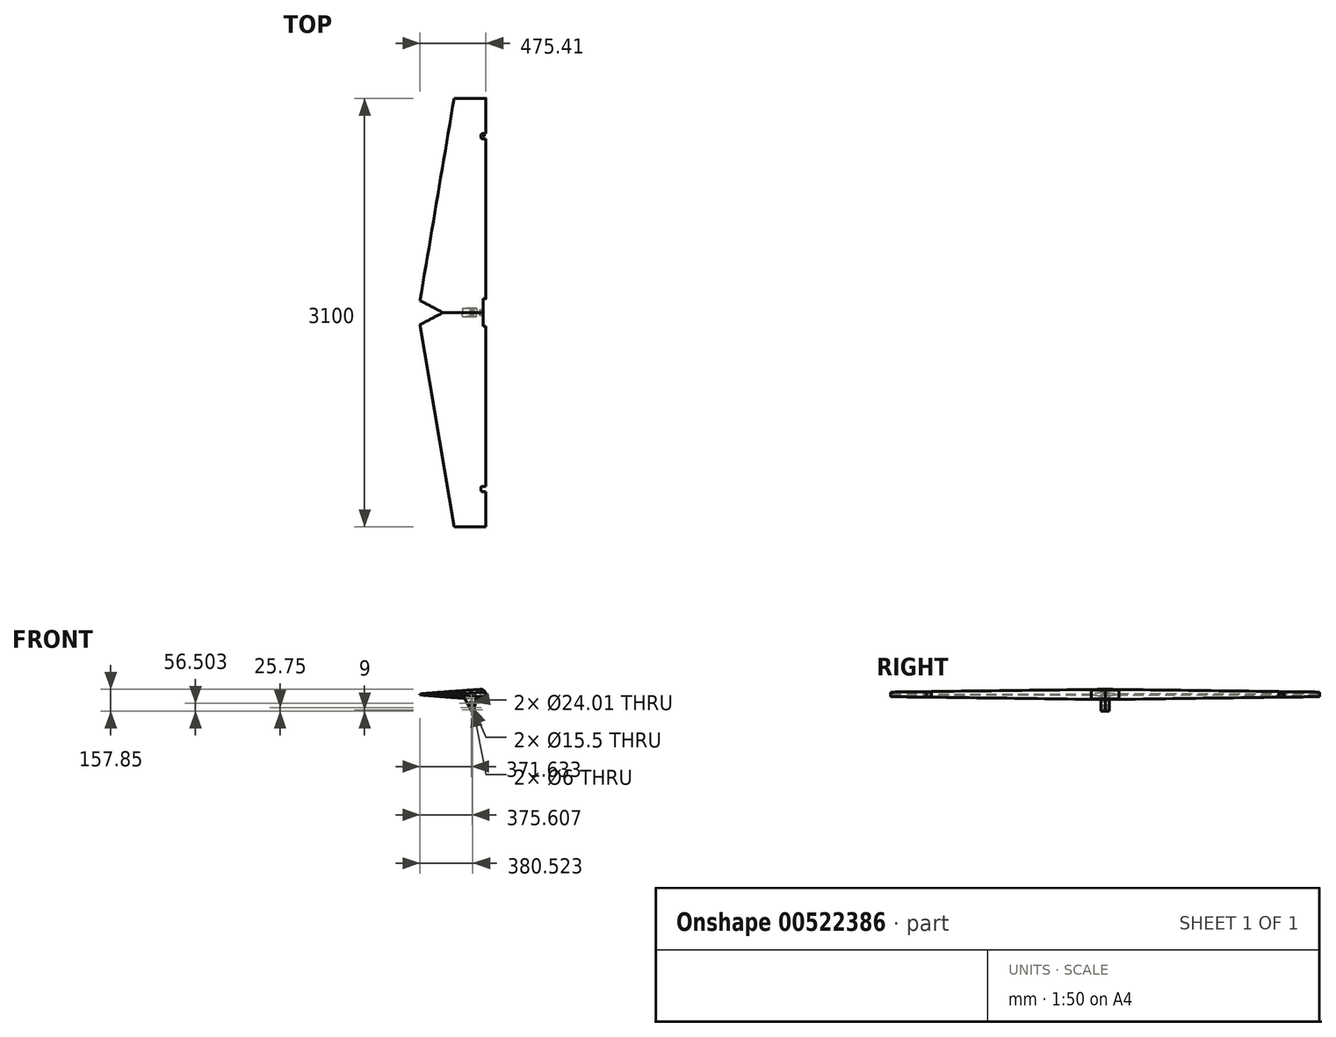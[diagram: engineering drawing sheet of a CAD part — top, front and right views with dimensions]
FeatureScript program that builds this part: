
annotation { "Feature Type Name" : "Feature", "Feature Type Description" : "" }
export const myFeature = defineFeature(function(context is Context, id is Id, definition is map)
    precondition{}
    {
        {
            var Q0;
            Q0=qCreatedBy(makeId("Top.planeOp"),FACE);
            var sketch = newSketch(context, id + "F0", { "sketchPlane" : qUnion([Q0])});
            skLineSegment(sketch, "E0.bottom", {"start": v(0, 0) * mm, "end": v(-490, 0) * mm});
            skLineSegment(sketch, "E0.top", {"start": v(0, -1550) * mm, "end": v(-230, -1550) * mm});
            skLineSegment(sketch, "E0.left", {"start": v(0, 0) * mm, "end": v(0, -1550) * mm});
            skLineSegment(sketch, "E0.right", {"start": v(-490, 0) * mm, "end": v(-230, -1550) * mm});
            skLineSegment(sketch, "E1", {"start": v(0, -100) * mm, "end": v(-20, -100) * mm});
            skLineSegment(sketch, "E2", {"start": v(-20, -100) * mm, "end": v(-20, 0) * mm});
            skLineSegment(sketch, "E3", {"start": v(-310, 0) * mm, "end": v(-475.4, -87) * mm});
            skLineSegment(sketch, "E4.bottom", {"start": v(0, -1295) * mm, "end": v(-36, -1295) * mm});
            skLineSegment(sketch, "E4.top", {"start": v(0, -1257) * mm, "end": v(-36, -1257) * mm});
            skLineSegment(sketch, "E4.left", {"start": v(0, -1295) * mm, "end": v(0, -1257) * mm});
            skLineSegment(sketch, "E4.right", {"start": v(-36, -1295) * mm, "end": v(-36, -1257) * mm});
            skSolve(sketch);
        }
        {
            var Q0;
            Q0=qCreatedBy(makeId("Front.planeOp"),FACE);
            var sketch = newSketch(context, id + "F1", { "sketchPlane" : qUnion([Q0])});
            skLineSegment(sketch, "E5", {"start": v(-39.56, 36.75) * mm, "end": v(-490, 3.5) * mm});
            skLineSegment(sketch, "E6", {"start": v(-490, 3.5) * mm, "end": v(-490, -3.5) * mm});
            skLineSegment(sketch, "E7", {"start": v(-490, -3.5) * mm, "end": v(-39.56, -36.75) * mm});
            skArc(sketch, "E8", {"start": v(-39.56, -36.75) * mm, "mid": v(0, 0) * mm, "end": v(-39.56, 36.75) * mm});
            skCircle(sketch, "E9", {"center": v(-36.85, 0) * mm, "radius": 5 * mm, "construction": true});
            skSolve(sketch);
        }
        {
            var Q0;
            Q0=sQuery(id+"F0.wireOp",VERTEX,"E0.left.end");
            var Q1;
            Q1=sQuery(id+"F0.wireOp",EDGE,"E0.left");
            cPlane(context, id + "F2", {"entities" : qUnion([Q0, Q1]), "cplaneType" : CPlaneType.LINE_POINT, "offset" : 25 * mm, "width" : 150 * mm, "height" : 150 * mm});
        }
        {
            var Q0;
            Q0=qCreatedBy(id+"F2.planeOp",FACE);
            var sketch = newSketch(context, id + "F3", { "sketchPlane" : qUnion([Q0])});
            skLineSegment(sketch, "E10", {"start": v(-17.62, 16.5) * mm, "end": v(-230, 2.5) * mm});
            skLineSegment(sketch, "E11", {"start": v(-230, 2.5) * mm, "end": v(-230, -2.5) * mm});
            skLineSegment(sketch, "E12", {"start": v(-230, -2.5) * mm, "end": v(-17.62, -16.5) * mm});
            skArc(sketch, "E13", {"start": v(-17.62, -16.5) * mm, "mid": v(0, 0) * mm, "end": v(-17.62, 16.5) * mm});
            skSolve(sketch);
        }
        {
            var Q0;
            Q0=makeQuery(id+"F3.imprint","IMPRINT",FACE,{"disambiguationData":[TD([[makeQuery(id+"F3.imprint","IMPRINT",EDGE,{"derivedFrom":sQuery(id+"F3.wireOp",EDGE,"E10")}),1.0]])]});
            var Q1;
            Q1=makeQuery(id+"F1.imprint","IMPRINT",FACE,{"disambiguationData":[TD([[makeQuery(id+"F1.imprint","IMPRINT",EDGE,{"derivedFrom":sQuery(id+"F1.wireOp",EDGE,"E5")}),1.0]])]});
            loft(context, id + "F4", {"sheetProfilesArray" : [{ "sheetProfileEntities" : qUnion([Q0]) }, { "sheetProfileEntities" : qUnion([Q1]) }]});
        }
        {
            var Q0;
            {var subQ4=sQuery(id+"F0.wireOp",EDGE,"E1");Q0=makeQuery(id+"F0.imprint","IMPRINT",FACE,{"disambiguationData":[TD([[makeQuery(id+"F0.imprint","IMPRINT",EDGE,{"derivedFrom":subQ4}),-1.0]])]});}
            extrude(context, id + "F5", {"entities" : qUnion([Q0]), "operationType" : NewBodyOperationType.REMOVE, "endBound" : BoundingType.SYMMETRIC, "depth" : 100 * mm, "offsetDistance" : 25 * mm});
        }
        {
            var Q0;
            {var subQ3=sQuery(id+"F0.wireOp",EDGE,"E3");Q0=makeQuery(id+"F0.imprint","IMPRINT",FACE,{"disambiguationData":[TD([[makeQuery(id+"F0.imprint","IMPRINT",EDGE,{"derivedFrom":subQ3}),-1.0]])]});}
            var Q1;
            Q1=sQuery(id+"F0.wireOp",EDGE,"E3");
            var Q2;
            Q2=sQuery(id+"F0.wireOp",EDGE,"E0.bottom");
            var Q3;
            Q3=sQuery(id+"F0.wireOp",EDGE,"E0.right");
            extrude(context, id + "F6", {"entities" : qUnion([Q0]), "operationType" : NewBodyOperationType.REMOVE, "surfaceEntities" : qUnion([Q1, Q2, Q3]), "endBound" : BoundingType.SYMMETRIC, "oppositeDirection" : true, "depth" : 60 * mm, "offsetDistance" : 25 * mm});
        }
        {
            var Q0;
            Q0=qCreatedBy(makeId("Front.planeOp"),FACE);
            var sketch = newSketch(context, id + "F7", { "sketchPlane" : qUnion([Q0])});
            skLineSegment(sketch, "E14", {"start": v(-66, 0) * mm, "end": v(-169, 0) * mm});
            skLineSegment(sketch, "E15", {"start": v(-169, 0) * mm, "end": v(-102.34, -121) * mm});
            skLineSegment(sketch, "E16", {"start": v(-102.34, -121) * mm, "end": v(-87.34, -121) * mm});
            skLineSegment(sketch, "E17", {"start": v(-87.34, -121) * mm, "end": v(-66, 0) * mm});
            skCircle(sketch, "E18", {"center": v(-38.5, 0) * mm, "radius": 5 * mm});
            skCircle(sketch, "E19", {"center": v(-103.78, -64.5) * mm, "radius": 12 * mm});
            skCircle(sketch, "E20", {"center": v(-99.8, -95.25) * mm, "radius": 7.75 * mm});
            skCircle(sketch, "E21", {"center": v(-94.89, -112) * mm, "radius": 3 * mm});
            skSolve(sketch);
        }
        {
            var Q0;
            Q0=makeQuery(id+"F7.imprint","IMPRINT",FACE,{"disambiguationData":[TD([[makeQuery(id+"F7.imprint","IMPRINT",EDGE,{"derivedFrom":sQuery(id+"F7.wireOp",EDGE,"E18")}),1.0]])]});
            extrude(context, id + "F8", {"entities" : qUnion([Q0]), "operationType" : NewBodyOperationType.ADD, "oppositeDirection" : true, "depth" : 19 * mm, "offsetDistance" : 25 * mm});
        }
        {
            var Q0;
            Q0=makeQuery(id+"F7.imprint","IMPRINT",FACE,{"disambiguationData":[TD([[makeQuery(id+"F7.imprint","IMPRINT",EDGE,{"derivedFrom":sQuery(id+"F7.wireOp",EDGE,"E14")}),1.0]])]});
            extrude(context, id + "F9", {"entities" : qUnion([Q0]), "operationType" : NewBodyOperationType.ADD, "oppositeDirection" : true, "depth" : 30 * mm, "offsetDistance" : 25 * mm});
        }
        {
            var Q0;
            Q0=qCreatedBy(id+"F2.planeOp",FACE);
            cPlane(context, id + "F10", {"entities" : qUnion([Q0]), "cplaneType" : CPlaneType.OFFSET, "offset" : 520 * mm, "oppositeDirection" : true, "width" : 150 * mm, "height" : 150 * mm});
        }
        {
            var Q0;
            Q0=makeQuery(id+"F0.imprint","IMPRINT",FACE,{"disambiguationData":[TD([[makeQuery(id+"F0.imprint","IMPRINT",EDGE,{"derivedFrom":sQuery(id+"F0.wireOp",EDGE,"E4.bottom")}),-1.0]])]});
            extrude(context, id + "F11", {"entities" : qUnion([Q0]), "operationType" : NewBodyOperationType.REMOVE, "endBound" : BoundingType.SYMMETRIC, "depth" : 100 * mm, "offsetDistance" : 25 * mm});
        }
        {
            var Q0;
            Q0=makeQuery(id+"F11.boolean.opBoolean","COPY",EDGE,{"derivedFrom":makeQuery(id+"F11.opExtrude","SWEPT_EDGE",EDGE,{"disambiguationData":[OSD([sQuery(id+"F0.wireOp",EDGE,"E4.bottom"),sQuery(id+"F0.wireOp",EDGE,"E4.right")])]})});
            var Q1;
            Q1=makeQuery(id+"F11.boolean.opBoolean","COPY",EDGE,{"derivedFrom":makeQuery(id+"F11.opExtrude","SWEPT_EDGE",EDGE,{"disambiguationData":[OSD([sQuery(id+"F0.wireOp",EDGE,"E4.top"),sQuery(id+"F0.wireOp",EDGE,"E4.right")])]})});
            fillet(context, id + "F12", {"entities" : qUnion([Q0, Q1]), "radius" : 12 * mm, "tangentPropagation" : true, "allowEdgeOverflow" : false});
        }
        {
            var Q0;
            Q0=makeQuery(id+"F4.opLoft","SWEPT_BODY",BODY,{"disambiguationData":[OSD([makeQuery(id+"F1.imprint","IMPRINT",FACE,{"disambiguationData":[TD([[makeQuery(id+"F1.imprint","IMPRINT",EDGE,{"derivedFrom":sQuery(id+"F1.wireOp",EDGE,"E5")}),1.0]])]}),makeQuery(id+"F3.imprint","IMPRINT",FACE,{"disambiguationData":[TD([[makeQuery(id+"F3.imprint","IMPRINT",EDGE,{"derivedFrom":sQuery(id+"F3.wireOp",EDGE,"E10")}),1.0]])]})])]});
            var Q1;
            Q1=qCreatedBy(makeId("Front.planeOp"),FACE);
            mirror(context, id + "F13", {"entities" : qUnion([Q0]), "mirrorPlane" : qUnion([Q1])});
        }
        {
            var Q0;
            Q0=makeQuery(id+"F13.opPattern","COPY",FACE,{"derivedFrom":makeQuery(id+"F11.boolean.opBoolean","COPY",FACE,{"derivedFrom":makeQuery(id+"F11.opExtrude","SWEPT_FACE",FACE,{"disambiguationData":[OSD([sQuery(id+"F0.wireOp",EDGE,"E4.bottom")])]})}),"instanceName":"1"});
            var sketch = newSketch(context, id + "F14", { "sketchPlane" : qUnion([Q0])});
            skCircle(sketch, "E22", {"center": v(-14, 0) * mm, "radius": 5 * mm});
            skFitSpline(sketch, "E23.0", {"points": [v(-36, 18.82) * mm, v(-31.07, 19.16) * mm, v(-26.15, 19.5) * mm, v(-19.87, 19.92) * mm, v(-18.5, 19.88) * mm, v(-15.8, 19.5) * mm, v(-14.47, 19.18) * mm, v(-11.91, 18.26) * mm, v(-10.68, 17.67) * mm, v(-8.36, 16.26) * mm, v(-7.28, 15.43) * mm, v(-5.3, 13.58) * mm, v(-4.4, 12.55) * mm, v(-2.84, 10.33) * mm, v(-2.18, 9.14) * mm, v(-1.1, 6.66) * mm, v(-0.69, 5.36) * mm, v(-0.14, 2.7) * mm, v(0, 1.35) * mm, v(0, -1.35) * mm, v(-0.14, -2.7) * mm, v(-0.69, -5.36) * mm, v(-1.1, -6.66) * mm, v(-2.18, -9.14) * mm, v(-2.84, -10.33) * mm, v(-4.4, -12.55) * mm, v(-5.3, -13.58) * mm, v(-7.28, -15.43) * mm, v(-8.36, -16.26) * mm, v(-10.68, -17.67) * mm, v(-11.91, -18.26) * mm, v(-14.47, -19.18) * mm, v(-15.8, -19.5) * mm, v(-18.5, -19.88) * mm, v(-19.87, -19.92) * mm, v(-26.15, -19.5) * mm, v(-31.07, -19.16) * mm, v(-36, -18.82) * mm]});
            skFitSpline(sketch, "E24", {"points": [v(-36, 18.82) * mm, v(-31.07, 19.16) * mm, v(-26.15, 19.5) * mm, v(-19.87, 19.92) * mm, v(-18.5, 19.88) * mm, v(-15.8, 19.5) * mm, v(-14.47, 19.18) * mm, v(-11.91, 18.26) * mm, v(-10.68, 17.67) * mm, v(-8.36, 16.26) * mm, v(-7.28, 15.43) * mm, v(-5.3, 13.58) * mm, v(-4.4, 12.55) * mm, v(-2.84, 10.33) * mm, v(-2.18, 9.14) * mm, v(-1.1, 6.66) * mm, v(-0.69, 5.36) * mm, v(-0.14, 2.7) * mm, v(0, 1.35) * mm, v(0, -1.35) * mm, v(-0.14, -2.7) * mm, v(-0.69, -5.36) * mm, v(-1.1, -6.66) * mm, v(-2.18, -9.14) * mm, v(-2.84, -10.33) * mm, v(-4.4, -12.55) * mm, v(-5.3, -13.58) * mm, v(-7.28, -15.43) * mm, v(-8.36, -16.26) * mm, v(-10.68, -17.67) * mm, v(-11.91, -18.26) * mm, v(-14.47, -19.18) * mm, v(-15.8, -19.5) * mm, v(-18.5, -19.88) * mm, v(-19.87, -19.92) * mm, v(-26.15, -19.5) * mm, v(-31.07, -19.16) * mm, v(-36, -18.82) * mm]});
            skLineSegment(sketch, "E25", {"start": v(-24, -19.64) * mm, "end": v(-24, 19.64) * mm});
            skSolve(sketch);
        }
        {
            var Q0;
            Q0=makeQuery(id+"F14.imprint","IMPRINT",FACE,{"disambiguationData":[TD([[makeQuery(id+"F14.imprint","IMPRINT",EDGE,{"derivedFrom":sQuery(id+"F14.wireOp",EDGE,"E22")}),1.0]])]});
            extrude(context, id + "F15", {"entities" : qUnion([Q0]), "operationType" : NewBodyOperationType.ADD, "depth" : 18 * mm, "offsetDistance" : 25 * mm});
        }
    });
